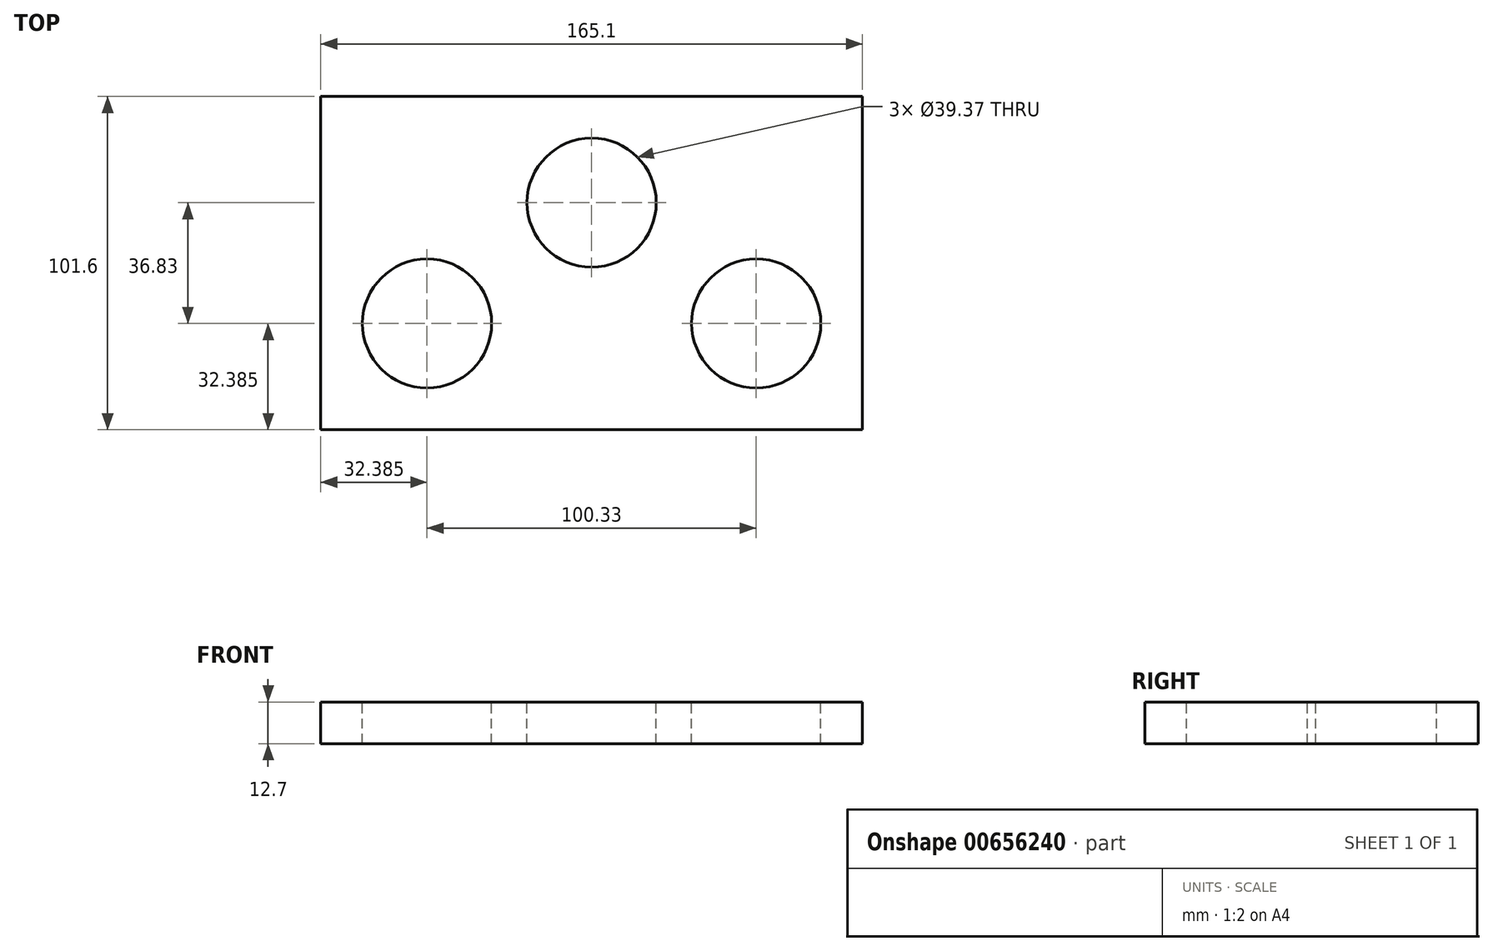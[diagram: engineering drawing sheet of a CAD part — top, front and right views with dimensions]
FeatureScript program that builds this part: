
annotation { "Feature Type Name" : "Feature", "Feature Type Description" : "" }
export const myFeature = defineFeature(function(context is Context, id is Id, definition is map)
    precondition{}
    {
        {
            var Q0;
            Q0=qCreatedBy(makeId("Top.planeOp"),FACE);
            var sketch = newSketch(context, id + "F0", { "sketchPlane" : qUnion([Q0])});
            skLineSegment(sketch, "E0.bottom", {"start": v(-82.55, -50.8) * mm, "end": v(82.55, -50.8) * mm});
            skLineSegment(sketch, "E0.top", {"start": v(-82.55, 50.8) * mm, "end": v(82.55, 50.8) * mm});
            skLineSegment(sketch, "E0.left", {"start": v(-82.55, -50.8) * mm, "end": v(-82.55, 50.8) * mm});
            skLineSegment(sketch, "E0.right", {"start": v(82.55, -50.8) * mm, "end": v(82.55, 50.8) * mm});
            skPoint(sketch, "E0.middle", {"position": v(0, 18.41) * mm});
            skCircle(sketch, "E1", {"center": v(-50.17, -18.41) * mm, "radius": 19.69 * mm});
            skCircle(sketch, "E2", {"center": v(0, 18.41) * mm, "radius": 19.69 * mm});
            skCircle(sketch, "E3", {"center": v(50.17, -18.41) * mm, "radius": 19.69 * mm});
            skSolve(sketch);
        }
        {
            var Q0;
            Q0=makeQuery(id+"F0.imprint","IMPRINT",FACE,{"disambiguationData":[TD([[makeQuery(id+"F0.imprint","IMPRINT",EDGE,{"derivedFrom":sQuery(id+"F0.wireOp",EDGE,"E0.bottom")}),1.0]])]});
            extrude(context, id + "F1", {"entities" : qUnion([Q0]), "oppositeDirection" : true, "depth" : 12.7 * mm, "offsetDistance" : 25.4 * mm});
        }
    });
